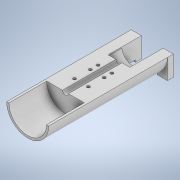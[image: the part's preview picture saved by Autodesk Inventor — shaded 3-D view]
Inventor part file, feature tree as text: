
AUTODESK INVENTOR PART (.ipt)
format: ipt  version: 2022 (Build 260153000, 153)  size: 385,024 bytes
history: native  units: mm
features: extrude x21, sketch x21, fillet x2
ambient origin geometry x8: Origin, YZ Plane, XZ Plane, XY Plane, X Axis, Y Axis, Z Axis, Center Point
bodies: Solid1 (feature_tree)
feature tree (44):
  extrude  "Extrusion1"  Depth=70.0mm
  extrude  "Extrusion2"  Depth=6.0mm TaperAngle=0.0deg
  extrude  "Extrusion3"  Depth=3.0mm
  fillet  "Fillet1"  Radius=40.0mm
  extrude  "Extrusion4"  Depth=4.0mm
  extrude  "Extrusion5"  Depth=5.0mm TaperAngle=0.0deg
  extrude  "Extrusion6"  Depth=11.0mm
  extrude  "Extrusion7"  Depth=11.0mm
  extrude  "Extrusion8"  Depth=24.0mm TaperAngle=0.0deg
  extrude  "Extrusion9"  Depth=6.0mm TaperAngle=0.0deg
  extrude  "Extrusion10"  Depth=13.8mm
  extrude  "Extrusion11"  Depth=13.8mm TaperAngle=0.0deg
  extrude  "Extrusion12"  Depth=50.0mm TaperAngle=0.0deg
  fillet  "Fillet3"  Radius=50.0mm
  extrude  "Extrusion19"  Depth=38.0mm
  extrude  "Extrusion20"  Depth=6.2mm TaperAngle=0.0deg
  extrude  "Extrusion21"  Depth=10.0mm TaperAngle=0.0deg
  extrude  "Extrusion22"  Depth=10.0mm TaperAngle=0.0deg
  extrude  "Extrusion23"  Depth=10.0mm TaperAngle=0.0deg
  extrude  "Extrusion24"  Depth=150.0mm TaperAngle=0.0deg
  extrude  "Extrusion25"  Depth=10.0mm TaperAngle=0.0deg
  extrude  "Extrusion27"  [1 undecoded]
  extrude  "Extrusion28"  [1 undecoded]
  sketch  "Sketch1"  dims[d0=62.0mm d1=70.0mm]
  sketch  "Sketch2"  dims[d2=6.0mm d3=40.0mm d4=0.0mm]
  sketch  "Sketch3"  dims[d5=62.0mm d9=3.0mm d10=40.0mm d12=360.0deg]
  sketch  "Sketch4"  dims[d14=40.0mm d15=0.0mm d16=4.0mm]
  sketch  "Sketch5"  dims[d18=11.5mm d19=5.0mm d20=0.0mm]
  sketch  "Sketch6"  dims[d21=8.0mm d22=11.0mm]
  sketch  "Sketch8"  dims[d23=11.0mm d24=5.0mm]
  sketch  "Sketch9"  dims[d25=5.0mm d26=24.0mm d27=0.0mm]
  sketch  "Sketch10"  dims[d29=6.0mm d30=6.0mm d31=0.0mm]
  sketch  "Sketch11"  dims[d32=13.8mm d33=0.0mm d37=33.7mm]
  sketch  "Sketch12"  dims[d38=11.0mm d39=13.8mm d40=0.0mm]
  sketch  "Sketch13"  dims[d41=6.0mm d42=50.0mm d43=0.0mm d44=50.0mm d45=0.0mm]
  sketch  "Sketch20"  dims[d47=36.0mm d48=0.0mm d49=38.0mm]
  sketch  "Sketch21"  dims[d50=32.0mm d51=0.0mm d52=6.2mm d53=0.0mm]
  sketch  "Sketch22"  dims[d63=1.0mm d69=10.0mm d70=0.0mm]
  sketch  "Sketch23"  dims[d71=10.0mm d72=0.0mm d73=10.0mm d74=0.0mm]
  sketch  "Sketch24"  dims[d75=10.0mm d76=0.0mm d77=10.0mm d78=0.0mm]
  sketch  "Sketch25"  dims[d79=150.0mm d80=0.0mm d81=150.0mm d82=0.0mm]
  sketch  "Sketch26"  dims[d90=0.0mm d91=0.0mm d92=10.0mm d93=0.0mm]
  sketch  "Sketch28"
  sketch  "Sketch29"
note: 2 required parameter values undecoded (feature->parameter linkage not recoverable at this tier; creation-order binding heuristic only, values carry confidence <= 0.55)
